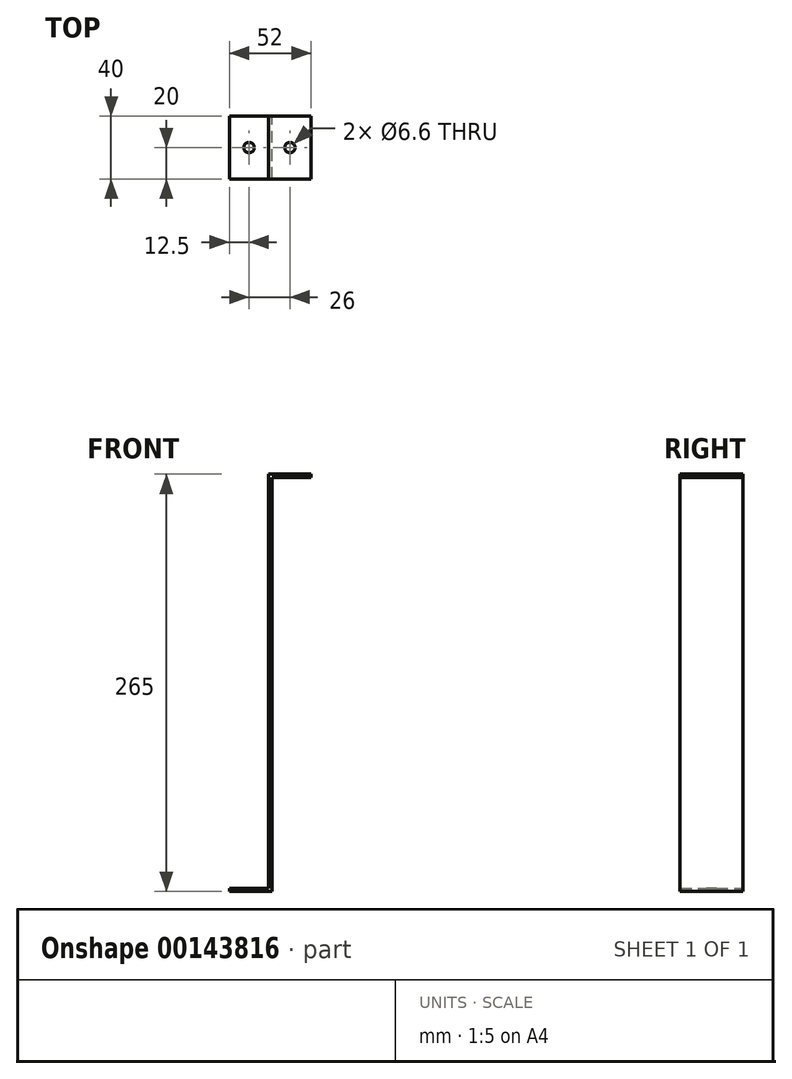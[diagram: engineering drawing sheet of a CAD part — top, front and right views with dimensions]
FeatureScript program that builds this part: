
annotation { "Feature Type Name" : "Feature", "Feature Type Description" : "" }
export const myFeature = defineFeature(function(context is Context, id is Id, definition is map)
    precondition{}
    {
        {
            var Q0;
            Q0=qCreatedBy(makeId("Front.planeOp"),FACE);
            var sketch = newSketch(context, id + "F0", { "sketchPlane" : qUnion([Q0])});
            skLineSegment(sketch, "E0", {"start": v(-25, -47.92) * mm, "end": v(0, -47.92) * mm});
            skLineSegment(sketch, "E1", {"start": v(0, -47.92) * mm, "end": v(0, 215.08) * mm});
            skLineSegment(sketch, "E2", {"start": v(0, 215.08) * mm, "end": v(27, 215.08) * mm});
            skLineSegment(sketch, "E3.0", {"start": v(2, 213.08) * mm, "end": v(27, 213.08) * mm});
            skLineSegment(sketch, "E3.1", {"start": v(2, -49.92) * mm, "end": v(2, 213.08) * mm});
            skLineSegment(sketch, "E3.2", {"start": v(-25, -49.92) * mm, "end": v(2, -49.92) * mm});
            skLineSegment(sketch, "E4", {"start": v(27, 215.08) * mm, "end": v(27, 213.08) * mm});
            skLineSegment(sketch, "E5", {"start": v(-25, -47.92) * mm, "end": v(-25, -49.92) * mm});
            skSolve(sketch);
        }
        {
            var Q0;
            Q0=makeQuery(id+"F0.imprint","IMPRINT",FACE,{"disambiguationData":[TD([[makeQuery(id+"F0.imprint","IMPRINT",EDGE,{"derivedFrom":sQuery(id+"F0.wireOp",EDGE,"E0")}),-1.0]])]});
            extrude(context, id + "F1", {"entities" : qUnion([Q0]), "endBound" : BoundingType.SYMMETRIC, "depth" : 40 * mm});
        }
        {
            var Q0;
            Q0=makeQuery(id+"F1.opExtrude","SWEPT_FACE",FACE,{"disambiguationData":[OSD([sQuery(id+"F0.wireOp",EDGE,"E2")])]});
            var sketch = newSketch(context, id + "F2", { "sketchPlane" : qUnion([Q0])});
            skPoint(sketch, "E6", {"position": v(13.5, 0) * mm});
            skPoint(sketch, "E6.positionSnap0", {"position": v(13.5, 20) * mm});
            skPoint(sketch, "E6.positionSnap1", {"position": v(27, 0) * mm});
            skSolve(sketch);
        }
        {
            var Q0;
            Q0=makeQuery(id+"F1.opExtrude","SWEPT_FACE",FACE,{"disambiguationData":[OSD([sQuery(id+"F0.wireOp",EDGE,"E0")])]});
            var sketch = newSketch(context, id + "F3", { "sketchPlane" : qUnion([Q0])});
            skPoint(sketch, "E7", {"position": v(-12.5, 20) * mm});
            skPoint(sketch, "E8", {"position": v(-12.5, 0) * mm});
            skPoint(sketch, "E8.positionSnap0", {"position": v(-25, 0) * mm});
            skSolve(sketch);
        }
        {
            var Q0;
            Q0=sQuery(id+"F2.wireOp",VERTEX,"E6");
            var Q1;
            Q1=sQuery(id+"F3.wireOp",VERTEX,"E8");
            var Q2;
            Q2=makeQuery(id+"F1.opExtrude","SWEPT_BODY",BODY,{"disambiguationData":[OSD([sQuery(id+"F0.wireOp",EDGE,"E0"),sQuery(id+"F0.wireOp",EDGE,"E1"),sQuery(id+"F0.wireOp",EDGE,"E2"),sQuery(id+"F0.wireOp",EDGE,"E3.0"),sQuery(id+"F0.wireOp",EDGE,"E3.1"),sQuery(id+"F0.wireOp",EDGE,"E3.2"),sQuery(id+"F0.wireOp",EDGE,"E4"),sQuery(id+"F0.wireOp",EDGE,"E5")])]});
            hole(context, id + "F4", {"style" : HoleStyle.SIMPLE, "endStyle" : HoleEndStyle.THROUGH, "standardTappedOrClearance" : lookupTablePath({ "standard" : "ISO", "fit" : "Normal", "size" : "M6", "type" : "Clearance" }), "standardBlindInLast" : lookupTablePath({ "fit" : "Standard", "standard" : "ISO", "size" : "M6", "type" : "Clearance" }), "holeDiameter" : 6.6 * mm, "locations" : qUnion([Q0, Q1]), "scope" : qUnion([Q2]), "isTappedThrough" : true});
        }
    });
